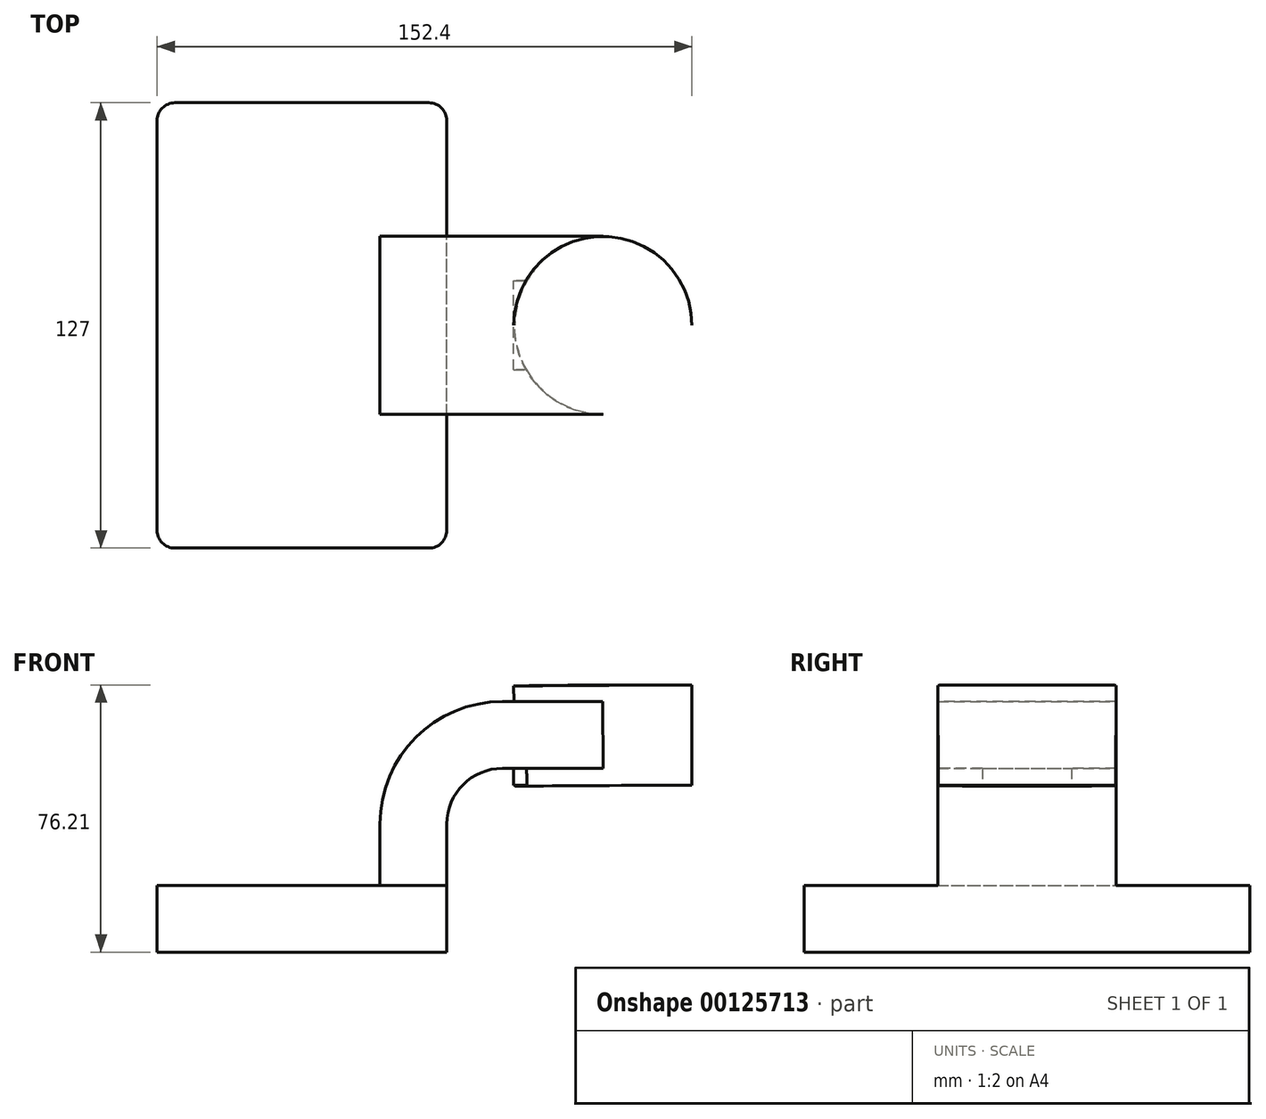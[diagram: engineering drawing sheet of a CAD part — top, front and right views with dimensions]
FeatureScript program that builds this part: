
annotation { "Feature Type Name" : "Feature", "Feature Type Description" : "" }
export const myFeature = defineFeature(function(context is Context, id is Id, definition is map)
    precondition{}
    {
        {
            var Q0;
            Q0=qCreatedBy(makeId("Front.planeOp"),FACE);
            var sketch = newSketch(context, id + "F0", { "sketchPlane" : qUnion([Q0])});
            skLineSegment(sketch, "E0.bottom", {"start": v(41.27, 9.53) * mm, "end": v(-41.28, 9.53) * mm});
            skLineSegment(sketch, "E0.top", {"start": v(41.28, -9.52) * mm, "end": v(-41.27, -9.52) * mm});
            skLineSegment(sketch, "E0.left", {"start": v(41.28, 9.53) * mm, "end": v(41.28, -9.52) * mm});
            skLineSegment(sketch, "E0.right", {"start": v(-41.28, 9.53) * mm, "end": v(-41.27, -9.52) * mm});
            skPoint(sketch, "E0.middle", {"position": v(0, 0) * mm});
            skLineSegment(sketch, "E1.bottom", {"start": v(111.12, 66.68) * mm, "end": v(60.32, 66.68) * mm});
            skLineSegment(sketch, "E1.top", {"start": v(111.13, 38.1) * mm, "end": v(60.33, 38.1) * mm});
            skLineSegment(sketch, "E1.left", {"start": v(111.12, 66.68) * mm, "end": v(111.13, 38.1) * mm});
            skLineSegment(sketch, "E1.right", {"start": v(60.32, 66.68) * mm, "end": v(60.33, 38.1) * mm});
            skPoint(sketch, "E1.middle", {"position": v(85.73, 52.39) * mm});
            skLineSegment(sketch, "E2", {"start": v(41.27, 9.53) * mm, "end": v(41.27, 27) * mm});
            skArc(sketch, "E3", {"start": v(41.27, 27) * mm, "mid": v(45.92, 38.23) * mm, "end": v(57.15, 42.88) * mm});
            skLineSegment(sketch, "E4", {"start": v(57.15, 42.88) * mm, "end": v(85.9, 42.88) * mm});
            skLineSegment(sketch, "E5.0", {"start": v(57.15, 61.93) * mm, "end": v(85.9, 61.93) * mm});
            skArc(sketch, "E5.1", {"start": v(22.22, 27) * mm, "mid": v(32.45, 51.7) * mm, "end": v(57.15, 61.93) * mm});
            skLineSegment(sketch, "E5.2", {"start": v(22.22, 9.53) * mm, "end": v(22.22, 27) * mm});
            skLineSegment(sketch, "E6", {"start": v(85.72, 66.68) * mm, "end": v(85.9, 38.1) * mm});
            skFitSpline(sketch, "E7", {"points": [v(-41.28, 9.53) * mm, v(57.15, 61.93) * mm], "startDerivative": vector(-0.5, 77.28) * mm, "endDerivative": vector(152.61, -2.2) * mm});
            skSolve(sketch);
        }
        {
            var Q0;
            Q0=makeQuery(id+"F0.imprint","IMPRINT",FACE,{"disambiguationData":[TD([[makeQuery(id+"F0.imprint","IMPRINT",EDGE,{"derivedFrom":sQuery(id+"F0.wireOp",EDGE,"E0.top")}),-1.0]])]});
            extrude(context, id + "F1", {"entities" : qUnion([Q0]), "endBound" : BoundingType.SYMMETRIC, "depth" : 127 * mm});
        }
        {
            var Q0;
            {var subQ0=sQuery(id+"F0.wireOp",EDGE,"E5.0");var subQ1=sQuery(id+"F0.wireOp",EDGE,"E1.right");var subQ2=makeQuery(id+"F0.imprint","INTERSECT",VERTEX,{"derivedFrom":[subQ1,subQ0]});Q0=makeQuery(id+"F0.imprint","IMPRINT",FACE,{"disambiguationData":[TD([[makeQuery(id+"F0.imprint","IMPRINT",EDGE,{"disambiguationData":[TD([[subQ2,-1.0]])],"derivedFrom":subQ1}),1.0]])]});}
            var Q1;
            {var subQ1=sQuery(id+"F0.wireOp",EDGE,"E2");Q1=makeQuery(id+"F0.imprint","IMPRINT",FACE,{"disambiguationData":[TD([[makeQuery(id+"F0.imprint","IMPRINT",EDGE,{"derivedFrom":subQ1}),1.0]])]});}
            extrude(context, id + "F2", {"entities" : qUnion([Q0, Q1]), "operationType" : NewBodyOperationType.ADD, "endBound" : BoundingType.SYMMETRIC, "depth" : 50.8 * mm});
        }
        {
            var Q0;
            Q0=makeQuery(id+"F1.opExtrude","CAP_EDGE",EDGE,{"disambiguationData":[OSD([sQuery(id+"F0.wireOp",EDGE,"E0.right")])],"isStart":false});
            var Q1;
            Q1=makeQuery(id+"F1.opExtrude","CAP_EDGE",EDGE,{"disambiguationData":[OSD([sQuery(id+"F0.wireOp",EDGE,"E0.left")])],"isStart":false});
            var Q2;
            Q2=makeQuery(id+"F1.opExtrude","CAP_EDGE",EDGE,{"disambiguationData":[OSD([sQuery(id+"F0.wireOp",EDGE,"E0.left")])],"isStart":true});
            var Q3;
            Q3=makeQuery(id+"F1.opExtrude","CAP_EDGE",EDGE,{"disambiguationData":[OSD([sQuery(id+"F0.wireOp",EDGE,"E0.right")])],"isStart":true});
            fillet(context, id + "F3", {"entities" : qUnion([Q0, Q1, Q2, Q3]), "radius" : 5.08 * mm, "tangentPropagation" : true, "allowEdgeOverflow" : false});
        }
        {
            var Q0;
            Q0=makeQuery(id+"F0.imprint","IMPRINT",FACE,{"disambiguationData":[TD([[makeQuery(id+"F0.imprint","IMPRINT",EDGE,{"derivedFrom":sQuery(id+"F0.wireOp",EDGE,"E0.top")}),-1.0]])]});
            var Q1;
            Q1=makeQuery(id+"F0.imprint","IMPRINT",FACE,{"disambiguationData":[TD([[makeQuery(id+"F0.imprint","IMPRINT",EDGE,{"derivedFrom":sQuery(id+"F0.wireOp",EDGE,"E5.1")}),1.0]])]});
            var Q2;
            {var subQ0=sQuery(id+"F0.wireOp",EDGE,"E1.right");var subQ1=sQuery(id+"F0.wireOp",EDGE,"E1.top");var subQ2=makeQuery(id+"F0.imprint","INTERSECT",VERTEX,{"derivedFrom":[subQ1,subQ0]});Q2=makeQuery(id+"F0.imprint","IMPRINT",FACE,{"disambiguationData":[TD([[makeQuery(id+"F0.imprint","IMPRINT",EDGE,{"disambiguationData":[TD([[subQ2,1.0]])],"derivedFrom":subQ1}),-1.0]])]});}
            var Q3;
            {var subQ1=sQuery(id+"F0.wireOp",EDGE,"E2");Q3=makeQuery(id+"F0.imprint","IMPRINT",FACE,{"disambiguationData":[TD([[makeQuery(id+"F0.imprint","IMPRINT",EDGE,{"derivedFrom":subQ1}),1.0]])]});}
            var Q4;
            {var subQ0=sQuery(id+"F0.wireOp",EDGE,"E5.0");var subQ1=sQuery(id+"F0.wireOp",EDGE,"E1.right");var subQ2=makeQuery(id+"F0.imprint","INTERSECT",VERTEX,{"derivedFrom":[subQ1,subQ0]});Q4=makeQuery(id+"F0.imprint","IMPRINT",FACE,{"disambiguationData":[TD([[makeQuery(id+"F0.imprint","IMPRINT",EDGE,{"disambiguationData":[TD([[subQ2,-1.0]])],"derivedFrom":subQ1}),1.0]])]});}
            extrude(context, id + "F4", {"entities" : qUnion([Q0, Q1, Q2, Q3, Q4]), "operationType" : NewBodyOperationType.ADD, "endBound" : BoundingType.SYMMETRIC, "depth" : 25.4 * mm});
        }
        {
            var Q0;
            {var subQ0=sQuery(id+"F0.wireOp",EDGE,"E1.left");Q0=makeQuery(id+"F0.imprint","IMPRINT",FACE,{"disambiguationData":[TD([[makeQuery(id+"F0.imprint","IMPRINT",EDGE,{"derivedFrom":subQ0}),-1.0]])]});}
            var Q1;
            Q1=sQuery(id+"F0.wireOp",EDGE,"E6");
            revolve(context, id + "F5", {"operationType" : NewBodyOperationType.ADD, "entities" : qUnion([Q0]), "axis" : qUnion([Q1]), "revolveType" : RevolveType.FULL});
        }
    });
